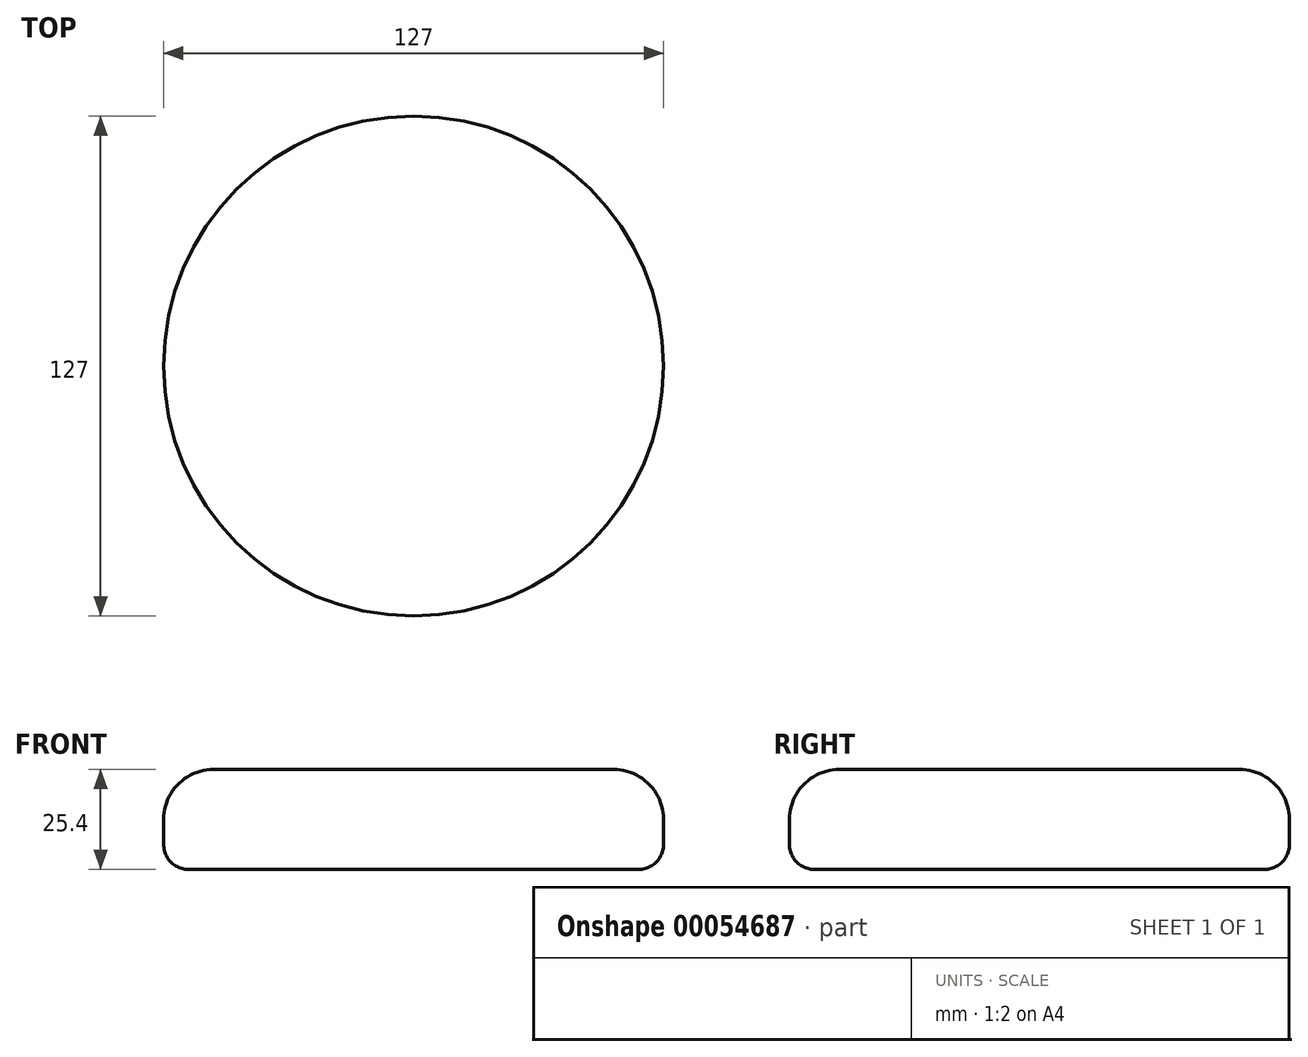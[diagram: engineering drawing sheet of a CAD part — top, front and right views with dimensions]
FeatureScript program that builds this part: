
annotation { "Feature Type Name" : "Feature", "Feature Type Description" : "" }
export const myFeature = defineFeature(function(context is Context, id is Id, definition is map)
    precondition{}
    {
        {
            var Q0;
            Q0=qCreatedBy(makeId("Top.planeOp"),FACE);
            var sketch = newSketch(context, id + "F0", { "sketchPlane" : qUnion([Q0])});
            skCircle(sketch, "E0", {"center": v(0, 0) * mm, "radius": 63.5 * mm});
            skSolve(sketch);
        }
        {
            var Q0;
            Q0=makeQuery(id+"F0.imprint","IMPRINT",FACE,{"disambiguationData":[TD([[makeQuery(id+"F0.imprint","IMPRINT",EDGE,{"derivedFrom":sQuery(id+"F0.wireOp",EDGE,"E0")}),1.0]])]});
            extrude(context, id + "F1", {"entities" : qUnion([Q0]), "depth" : 25.4 * mm});
        }
        {
            var Q0;
            Q0=makeQuery(id+"F1.opExtrude","CAP_EDGE",EDGE,{"disambiguationData":[OSD([sQuery(id+"F0.wireOp",EDGE,"E0")])],"isStart":false});
            fillet(context, id + "F2", {"entities" : qUnion([Q0]), "radius" : 12.7 * mm, "tangentPropagation" : true, "allowEdgeOverflow" : false});
        }
        {
            var Q0;
            Q0=makeQuery(id+"F1.opExtrude","CAP_EDGE",EDGE,{"disambiguationData":[OSD([sQuery(id+"F0.wireOp",EDGE,"E0")])],"isStart":true});
            fillet(context, id + "F3", {"entities" : qUnion([Q0]), "radius" : 6.35 * mm, "tangentPropagation" : true, "allowEdgeOverflow" : false});
        }
    });
